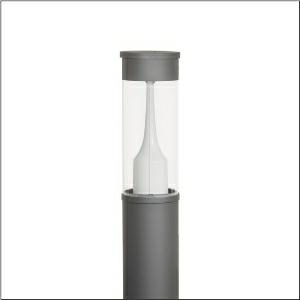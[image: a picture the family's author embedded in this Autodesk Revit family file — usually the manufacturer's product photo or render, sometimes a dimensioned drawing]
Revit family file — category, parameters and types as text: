
# Revit family: city-light_260_iq___st1_2a_5xa5295kf14h_47e0
name_source: partatom
category: Lighting Fixtures
units: mm (PartAtom-declared; Revit-internal decimal feet)

## family parameters
Cut with Voids When Loaded = No
Host = Face
Light Source = No
Part Type = Normal
Room Calculation Point = No
Round Connector Dimension = Use Diameter
Shared = No

## types (1)
- --- (1 x LED, 1540 lm, 10 W, 4000K)
    Apparent Load = 10 VA
    CIE Flux Codes = 22 61 93 96 100
    Color Rendering = 70
    Color Temperature = 4000K
    Default Elevation = 1800 mm
    Description = City-Light 260 iQ, light pillar, Module 540 iQ-SR, primary light control with 3 zone facetted reflector, of plastic, silver coated, highly specular, structured, primary optical cover: cover, of PMMA, transparent, partly coated, light distribution: ST1.2a, primary light characteristic: asymmetric, LED, High Power LED, rated luminous flux: 1.540lm, luminous efficacy: 154lm/W, light colour: 740, colour temperature: 4000K, control gear: iQ Street-Remote, control: pre-setting: logarithmic dimming characteristic, Street-Remote, Auto-Match, Temp-Guard, Lumen-Switch, Night-Set, Smart-Wire, Light-Fading, Desk-Remote (wireless, voltage-free reading and setting of iQ features in the workshop via application-optimized NFC function/RFID function), optimised constant luminous flux control (CLO 2.0), with terminal, 6-pole, max. 2.5mm², mains connection: 230..240V, AC, 50/60Hz, start of lifetime: 10W, end of service life: 10W, reduction: 5W, luminaire housing, cylindrical, of extruded aluminium section, coated, Siteco® metallic grey (DB 702S), length: 2.600mm, diameter: 200mm, Module 540 iQ-SR, traffic white (RAL 9016), equipment: standard, protection rating (complete): IP65, insulation class (complete): insulation class II (safety insulation), certification: CE, ENEC, VDE, packaging unit: 1 piece

Light Distribution: ST1.2a
    Height = 500 mm
    Lamp = 1 x LED
    Lamp Light Flux = 1540 lm
    Lamp Power = 10 W
    Lamp count = 1
    Length = 200 mm  [stored 0.656168 ft]
    Luminous efficacy = 154 lm/W
    Manufacturer = Siteco
    ModVariant = No
    Model = 5XA5295KF14H
    Mounting Place = Floor
    Mounting Type = Freestanding
    Number of Poles = 1
    OnlyDefault = Yes
    Power Factor = 1
    Product Name = City-Light 260 iQ | ST1.2a
    Product group = light pillar
    ProductGroupID = 1301
    Protection Class = Protection class II
    Protection Degree = IP 65
    RLX_Detail_Level = 1
    RLX_Emergency_Light_Flux = 0 lm
    RLX_Emergency_Type = 0
    RLX_Emergency_Type_DB = No
    RlxData = <blob elided: 64689 chars, md5=42d1e204>
    Socket = socket
    Standby Power = 0 W
    System Light Flux = 1540 lm
    System Power = 10 W
    Type Comments = factory setting: luminous flux: 100 % | dim-lin: 254 | 401 mA
    Type Image = l_1006918.jpg
    URL = http://relux.com
    VarID = @adj_158649
    Voltage = 0 V
    Weight = 0.00 kg
    Width = 0 mm  [stored 0 ft]

note: [stored X ft] marks values corroborated as IEEE doubles in the binary element streams (Revit-internal decimal feet)

## geometry (parser evidence)
native form markers: Blend x4, Sweep x8
no freeform markers — native parametric forms only
